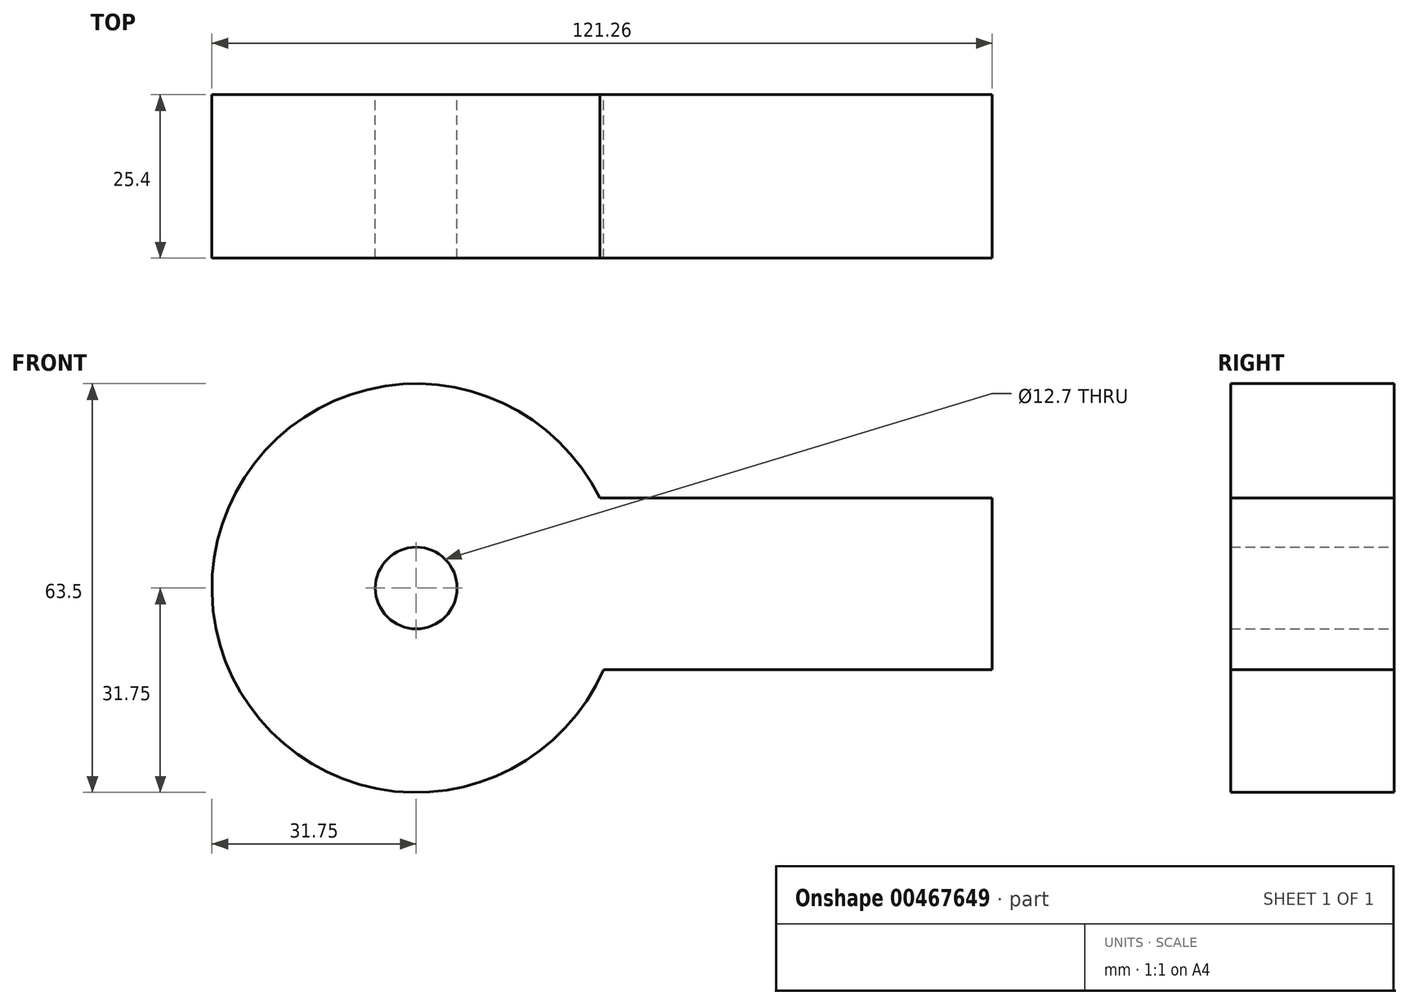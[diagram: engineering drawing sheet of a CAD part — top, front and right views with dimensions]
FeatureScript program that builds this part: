
annotation { "Feature Type Name" : "Feature", "Feature Type Description" : "" }
export const myFeature = defineFeature(function(context is Context, id is Id, definition is map)
    precondition{}
    {
        {
            var Q0;
            Q0=qCreatedBy(makeId("Front.planeOp"),FACE);
            var sketch = newSketch(context, id + "F0", { "sketchPlane" : qUnion([Q0])});
            skCircle(sketch, "E0", {"center": v(0, 0) * mm, "radius": 31.75 * mm});
            skLineSegment(sketch, "E1", {"start": v(28.51, 13.96) * mm, "end": v(89.5, 13.96) * mm});
            skLineSegment(sketch, "E2", {"start": v(89.5, 13.96) * mm, "end": v(89.5, -12.66) * mm});
            skLineSegment(sketch, "E3", {"start": v(89.5, -12.66) * mm, "end": v(29.12, -12.66) * mm});
            skCircle(sketch, "E4", {"center": v(0, 0) * mm, "radius": 6.35 * mm});
            skSolve(sketch);
        }
        {
            var Q0;
            Q0 = qSketchRegion(id + "F0", true);
            extrude(context, id + "F1", {"entities" : qUnion([Q0]), "depth" : 25.4 * mm});
        }
        {
            var Q0;
            Q0=makeQuery(id+"F1.opExtrude","CAP_FACE",FACE,{"disambiguationData":[OSD([sQuery(id+"F0.wireOp",EDGE,"E0"),sQuery(id+"F0.wireOp",EDGE,"E1"),sQuery(id+"F0.wireOp",EDGE,"E2"),sQuery(id+"F0.wireOp",EDGE,"E3"),sQuery(id+"F0.wireOp",EDGE,"E4")])],"isStart":false});
            extrude(context, id + "F2", {"entities" : qUnion([Q0]), "operationType" : NewBodyOperationType.ADD, "oppositeDirection" : true, "depth" : 13.97 * mm});
        }
    });
